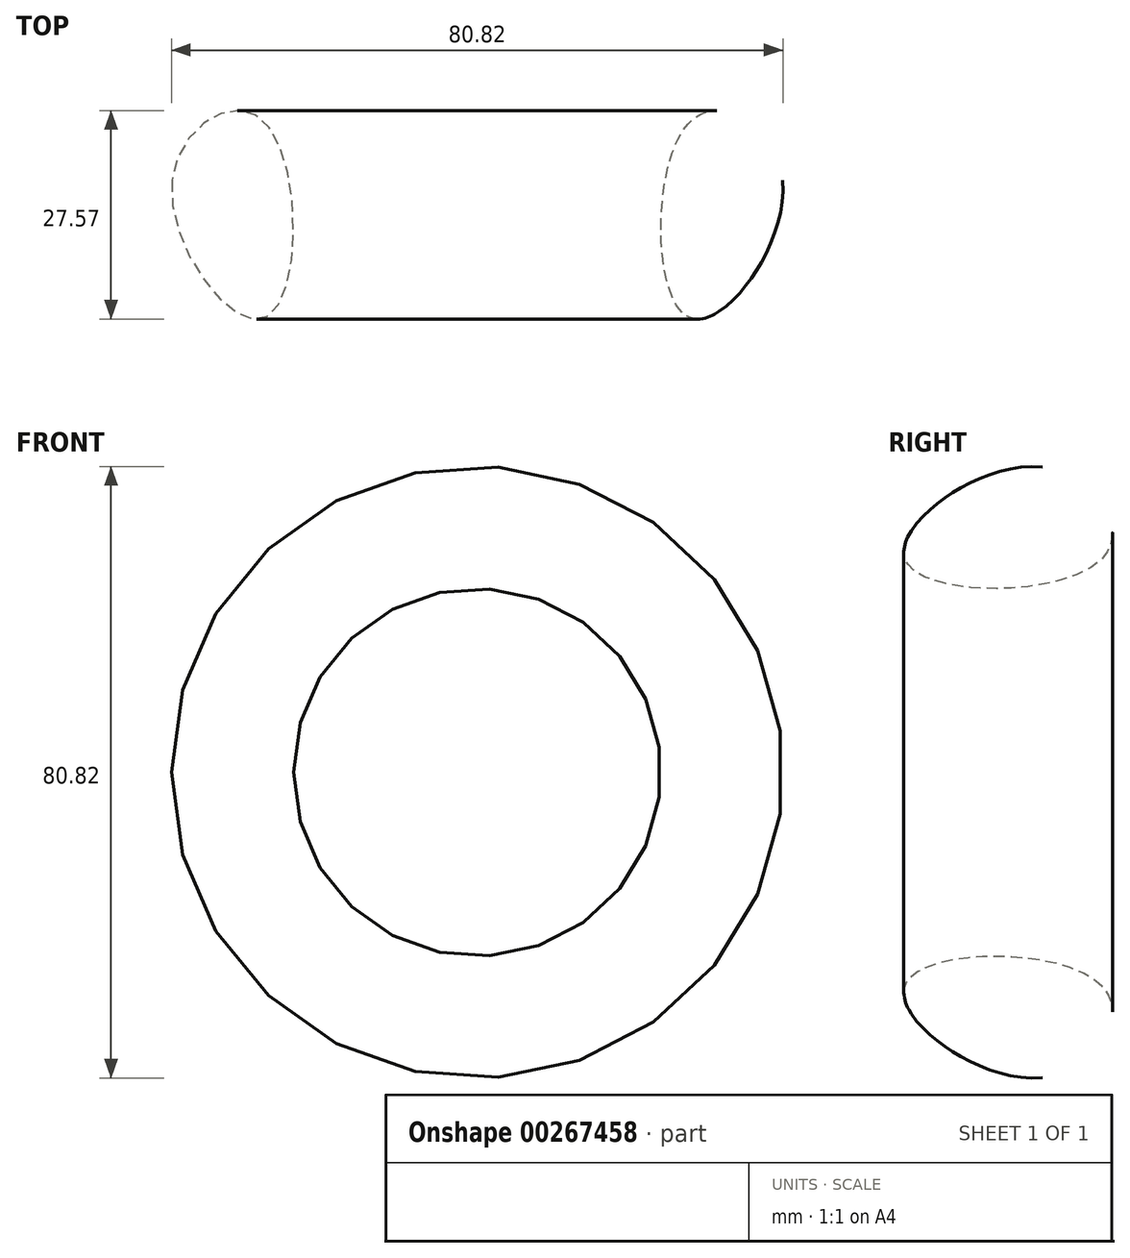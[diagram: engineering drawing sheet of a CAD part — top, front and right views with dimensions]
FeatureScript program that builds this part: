
annotation { "Feature Type Name" : "Feature", "Feature Type Description" : "" }
export const myFeature = defineFeature(function(context is Context, id is Id, definition is map)
    precondition{}
    {
        {
            var Q0;
            Q0=qCreatedBy(makeId("Top.planeOp"),FACE);
            var sketch = newSketch(context, id + "F0", { "sketchPlane" : qUnion([Q0])});
            skFitSpline(sketch, "E0", {"points": [v(-40.35, 34.13) * mm, v(-27.91, 16.1) * mm, v(-28.52, 42.26) * mm, v(-40.35, 34.13) * mm]});
            skLineSegment(sketch, "E1", {"start": v(0, 77.02) * mm, "end": v(0, -78.73) * mm});
            skSolve(sketch);
        }
        {
            var Q0;
            Q0=makeQuery(id+"F0.imprint","IMPRINT",FACE,{"disambiguationData":[TD([[makeQuery(id+"F0.imprint","IMPRINT",EDGE,{"derivedFrom":sQuery(id+"F0.wireOp",EDGE,"E0")}),1.0]])]});
            var Q1;
            Q1=sQuery(id+"F0.wireOp",EDGE,"E1");
            revolve(context, id + "F1", {"entities" : qUnion([Q0]), "axis" : qUnion([Q1]), "revolveType" : RevolveType.SYMMETRIC, "oppositeDirection" : true, "angle" : 360 * degree});
        }
    });
